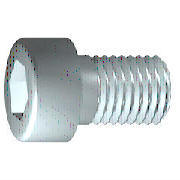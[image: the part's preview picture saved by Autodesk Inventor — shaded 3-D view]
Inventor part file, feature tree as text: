
AUTODESK INVENTOR PART (.ipt)
format: ipt  version: 2020 (Build 240168000, 168)  size: 192,512 bytes
history: native  units: mm (DEFAULTED — no unit token found)
features: sketch x2, other x1, extrude x1, plane x1, fillet x1
ambient origin geometry x7: Origin, YZ Plane, XY Plane, X Axis, Y Axis, Z Axis, Center Point
bodies: Solid1 (feature_tree)
feature tree (6):
  other  "Körper"
  extrude  "Loch"  Depth=2.0mm
  plane  "Work Plane1"
  fillet  "Fillet2"  Radius=2.0mm
  sketch  "Skizze1"  dims[d1=8.8mm d2=0.24548mm d3=2.0mm]
  sketch  "Skizze2"  dims[d4=1.0mm d5=60.0deg d6=2.0mm d7=2.0mm d8=1.732051mm d9=3.8mm d10=90.0deg d11=10.0mm d12=0.0mm d13=8.8mm d14=0.0mm d15=0.24538mm d16=0.24538mm d17=0.2mm d19=0.0mm d26=10.0mm d27=45.0deg d28=0.0mm d29=0.0mm d30=0.1mm]
